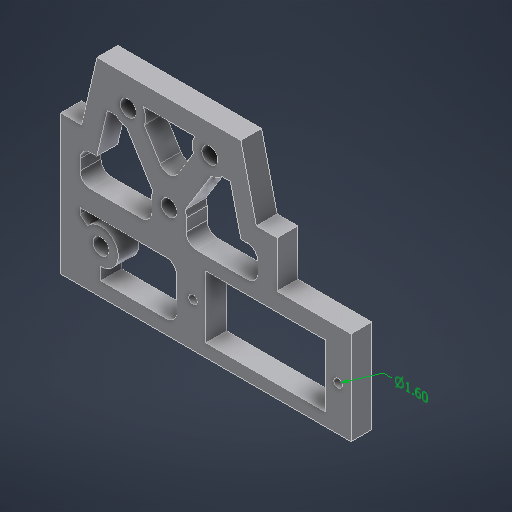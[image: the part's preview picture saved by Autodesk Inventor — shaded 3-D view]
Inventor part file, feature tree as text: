
AUTODESK INVENTOR PART (.ipt)
format: ipt  version: 2025.3 (Build 293356000, 356)  size: 337,920 bytes
history: native  units: in
note: dims shown in document units (in); Inventor stores cm internally (conversion verified against a paired STEP export)
features: extrude x6, sketch x4, fillet x3, other x2, direct_edit x1, move_body x1
ambient origin geometry x8: Origin, YZ Plane, XZ Plane, XY Plane, X Axis, Y Axis, Z Axis, Center Point
bodies: Solid1 (feature_tree)
feature tree (17):
  other  "Annotations"
  extrude  "Extrusion1"  Depth=0.1575in TaperAngle=0.0deg
  extrude  "Extrusion3"  Depth=0.3937in TaperAngle=0.0deg
  extrude  "Extrusion4"  Depth=0.3937in TaperAngle=0.0deg
  extrude  "Extrusion6"  Depth=0.0787in
  extrude  "Extrusion7"  Depth=0.3047in
  extrude  "Extrusion8"  Depth=0.3937in TaperAngle=0.0deg
  fillet  "Fillet1"  Radius=0.1181in
  fillet  "Fillet2"  Radius=0.7169in
  fillet  "Fillet3"  Radius=0.8217in
  direct_edit  "Direct Edit2"
  sketch  "Sketch1"  dims[d4=0.063in d5=0.063in d14=0.1575in d15=0.0in]
  sketch  "Sketch3"  dims[d21=0.1181in d24=0.3937in d25=0.0in]
  sketch  "Sketch4"  dims[d29=0.1181in d32=0.3937in d33=0.0in]
  sketch  "Sketch8"  dims[d49=0.1181in d50=0.374in d51=0.3047in d52=0.3937in d53=0.0in d54=0.1181in d55=0.7169in d56=0.8217in d57=0.3937in d58=0.0in d59=0.2638in d60=0.2638in d61=0.2638in d65=0.2638in d66=0.0787in d67=0.0787in d68=0.3937in d69=0.0in d70=0.0787in d71=0.0787in d72=0.0787in d76=0.0in d77=0.0in d78=-0.0394in d79=2.4516in d80=0.063in]
  move_body  "Move2"
  other  "Diameter Dimension 1"
